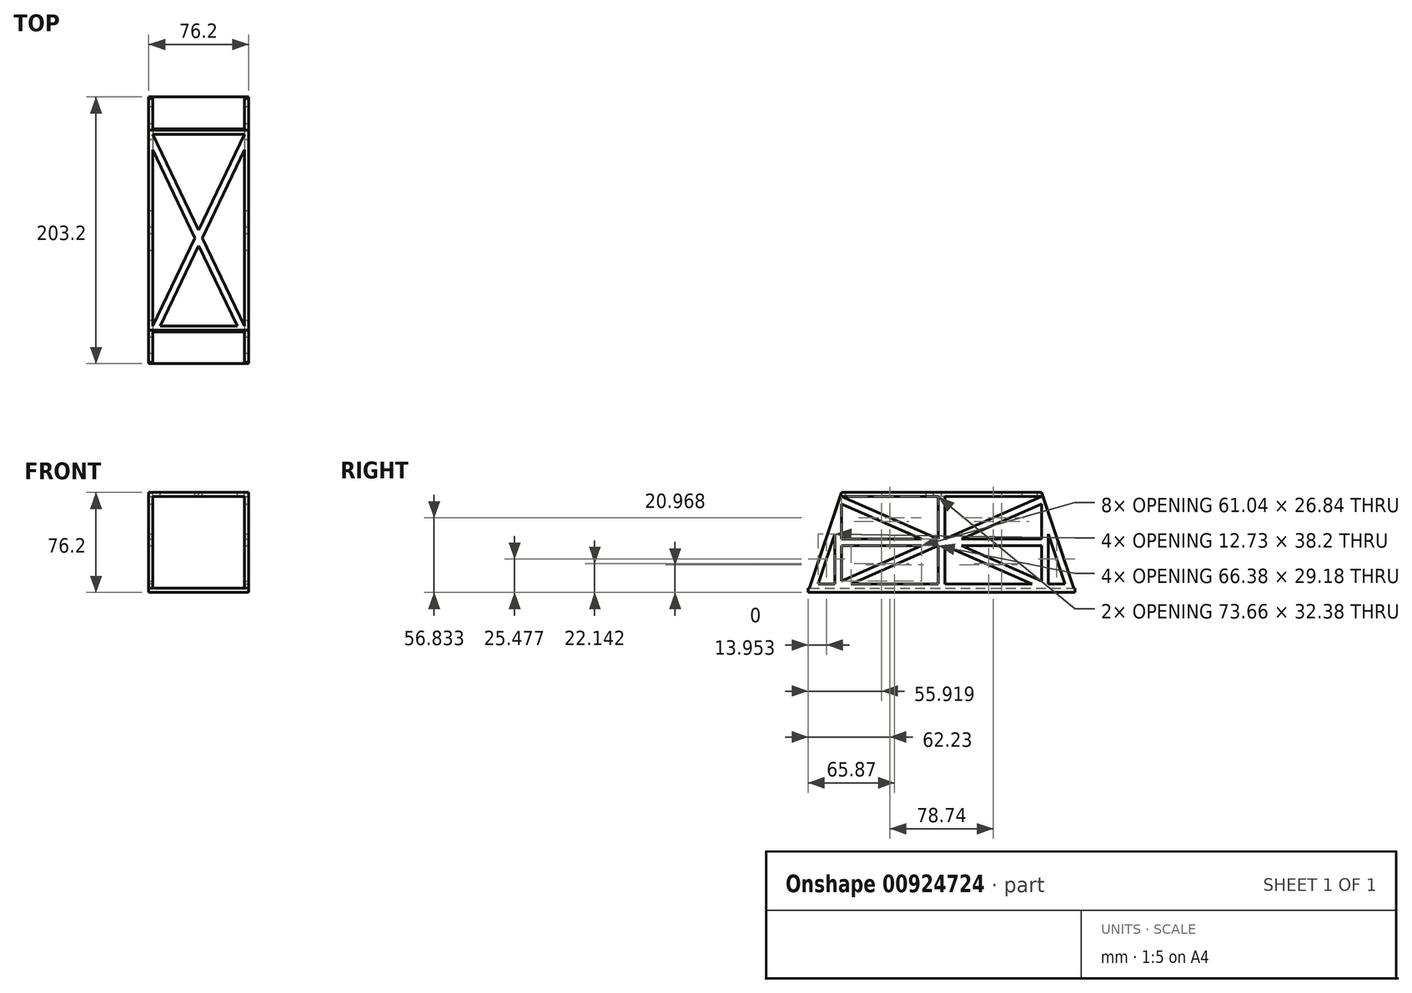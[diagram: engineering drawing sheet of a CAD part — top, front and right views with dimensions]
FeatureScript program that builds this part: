
annotation { "Feature Type Name" : "Feature", "Feature Type Description" : "" }
export const myFeature = defineFeature(function(context is Context, id is Id, definition is map)
    precondition{}
    {
        {
            var Q0;
            Q0=qCreatedBy(makeId("Right.planeOp"),FACE);
            var sketch = newSketch(context, id + "F0", { "sketchPlane" : qUnion([Q0])});
            skLineSegment(sketch, "E0", {"start": v(-101.6, -38.1) * mm, "end": v(101.6, -38.1) * mm});
            skLineSegment(sketch, "E1", {"start": v(-76.2, 38.1) * mm, "end": v(76.2, 38.1) * mm});
            skLineSegment(sketch, "E2", {"start": v(-76.2, 38.1) * mm, "end": v(-101.6, -38.1) * mm});
            skLineSegment(sketch, "E3", {"start": v(76.2, 38.1) * mm, "end": v(101.6, -38.1) * mm});
            skSolve(sketch);
        }
        {
            var Q0;
            Q0=makeQuery(id+"F0.imprint","IMPRINT",FACE,{"disambiguationData":[TD([[makeQuery(id+"F0.imprint","IMPRINT",EDGE,{"derivedFrom":sQuery(id+"F0.wireOp",EDGE,"E0")}),1.0]])]});
            extrude(context, id + "F1", {"entities" : qUnion([Q0]), "endBound" : BoundingType.SYMMETRIC, "depth" : 76.2 * mm, "offsetDistance" : 25.4 * mm});
        }
        {
            var Q0;
            Q0=makeQuery(id+"F1.opExtrude","CAP_FACE",FACE,{"disambiguationData":[OSD([sQuery(id+"F0.wireOp",EDGE,"E0"),sQuery(id+"F0.wireOp",EDGE,"E1"),sQuery(id+"F0.wireOp",EDGE,"E2"),sQuery(id+"F0.wireOp",EDGE,"E3")])],"isStart":false});
            var sketch = newSketch(context, id + "F2", { "sketchPlane" : qUnion([Q0])});
            skLineSegment(sketch, "E4.bottom", {"start": v(76.2, -34.92) * mm, "end": v(-76.2, -34.92) * mm});
            skLineSegment(sketch, "E4.top", {"start": v(76.2, 34.92) * mm, "end": v(-76.2, 34.92) * mm});
            skLineSegment(sketch, "E4.left", {"start": v(76.2, -34.92) * mm, "end": v(76.2, 34.92) * mm});
            skLineSegment(sketch, "E4.right", {"start": v(-76.2, -34.92) * mm, "end": v(-76.2, 34.92) * mm});
            skPoint(sketch, "E4.middle", {"position": v(0, 0) * mm});
            skLineSegment(sketch, "E5.bottom", {"start": v(2.54, -34.92) * mm, "end": v(-2.54, -34.92) * mm});
            skLineSegment(sketch, "E5.top", {"start": v(2.54, 34.92) * mm, "end": v(-2.54, 34.92) * mm});
            skLineSegment(sketch, "E5.left", {"start": v(2.54, -34.93) * mm, "end": v(2.54, 34.93) * mm});
            skLineSegment(sketch, "E5.right", {"start": v(-2.54, -34.93) * mm, "end": v(-2.54, 34.93) * mm});
            skLineSegment(sketch, "E6", {"start": v(-2.54, 0) * mm, "end": v(2.54, 0) * mm});
            skLineSegment(sketch, "E7.bottom", {"start": v(76.2, -2.54) * mm, "end": v(-76.2, -2.54) * mm});
            skLineSegment(sketch, "E7.top", {"start": v(76.2, 2.54) * mm, "end": v(-76.2, 2.54) * mm});
            skLineSegment(sketch, "E7.left", {"start": v(76.2, -2.54) * mm, "end": v(76.2, 2.54) * mm});
            skLineSegment(sketch, "E7.right", {"start": v(-76.2, -2.54) * mm, "end": v(-76.2, 2.54) * mm});
            skLineSegment(sketch, "E8", {"start": v(-76.2, 34.92) * mm, "end": v(-2.54, 2.54) * mm});
            skLineSegment(sketch, "E9", {"start": v(2.54, 2.54) * mm, "end": v(76.2, 34.92) * mm});
            skLineSegment(sketch, "E10", {"start": v(2.54, -2.54) * mm, "end": v(76.2, -34.92) * mm});
            skLineSegment(sketch, "E11", {"start": v(-2.54, -2.54) * mm, "end": v(-76.2, -34.92) * mm});
            skLineSegment(sketch, "E12", {"start": v(-76.2, -29.38) * mm, "end": v(-15.16, -2.54) * mm});
            skLineSegment(sketch, "E13", {"start": v(-15.16, 2.54) * mm, "end": v(-76.2, 29.38) * mm});
            skLineSegment(sketch, "E14", {"start": v(15.16, 2.54) * mm, "end": v(76.2, 29.38) * mm});
            skLineSegment(sketch, "E15", {"start": v(15.16, -2.54) * mm, "end": v(76.2, -29.38) * mm});
            skLineSegment(sketch, "E16", {"start": v(-81.28, -34.92) * mm, "end": v(-81.28, 6.48) * mm});
            skLineSegment(sketch, "E17", {"start": v(-81.28, 6.48) * mm, "end": v(-95.08, -34.92) * mm});
            skLineSegment(sketch, "E18", {"start": v(-95.08, -34.92) * mm, "end": v(-81.28, -34.92) * mm});
            skLineSegment(sketch, "E19.MirrorCS", {"start": v(81.28, -34.92) * mm, "end": v(81.28, 6.48) * mm});
            skLineSegment(sketch, "E20.MirrorCS", {"start": v(81.28, 6.48) * mm, "end": v(95.08, -34.92) * mm});
            skLineSegment(sketch, "E21.MirrorCS", {"start": v(95.08, -34.92) * mm, "end": v(81.28, -34.92) * mm});
            skSolve(sketch);
        }
        {
            var Q0;
            Q0=qCreatedBy(makeId("Front.planeOp"),FACE);
            var sketch = newSketch(context, id + "F3", { "sketchPlane" : qUnion([Q0])});
            skLineSegment(sketch, "E22.bottom", {"start": v(-34.93, -34.93) * mm, "end": v(34.93, -34.93) * mm});
            skLineSegment(sketch, "E22.top", {"start": v(-34.93, 34.93) * mm, "end": v(34.93, 34.93) * mm});
            skLineSegment(sketch, "E22.left", {"start": v(-34.93, -34.93) * mm, "end": v(-34.93, 34.93) * mm});
            skLineSegment(sketch, "E22.right", {"start": v(34.92, -34.93) * mm, "end": v(34.92, 34.93) * mm});
            skPoint(sketch, "E22.middle", {"position": v(0, 0) * mm});
            skSolve(sketch);
        }
        {
            var Q0;
            Q0=qSketchRegion(id+"F3",true);
            extrude(context, id + "F4", {"entities" : qUnion([Q0]), "operationType" : NewBodyOperationType.REMOVE, "endBound" : BoundingType.SYMMETRIC, "depth" : 254 * mm, "offsetDistance" : 25.4 * mm});
        }
        {
            var Q0;
            Q0=makeQuery(id+"F2.imprint","IMPRINT",FACE,{"disambiguationData":[TD([[makeQuery(id+"F2.imprint","IMPRINT",EDGE,{"derivedFrom":sQuery(id+"F2.wireOp",EDGE,"E16")}),1.0]])]});
            var Q1;
            {var subQ3=sQuery(id+"F2.wireOp",EDGE,"E12");Q1=makeQuery(id+"F2.imprint","IMPRINT",FACE,{"disambiguationData":[TD([[makeQuery(id+"F2.imprint","IMPRINT",EDGE,{"derivedFrom":subQ3}),1.0]])]});}
            var Q2;
            {var subQ3=sQuery(id+"F2.wireOp",EDGE,"E13");Q2=makeQuery(id+"F2.imprint","IMPRINT",FACE,{"disambiguationData":[TD([[makeQuery(id+"F2.imprint","IMPRINT",EDGE,{"derivedFrom":subQ3}),1.0]])]});}
            var Q3;
            {var subQ0=sQuery(id+"F2.wireOp",EDGE,"E8");Q3=makeQuery(id+"F2.imprint","IMPRINT",FACE,{"disambiguationData":[TD([[makeQuery(id+"F2.imprint","IMPRINT",EDGE,{"derivedFrom":subQ0}),1.0]])]});}
            var Q4;
            {var subQ0=sQuery(id+"F2.wireOp",EDGE,"E9");Q4=makeQuery(id+"F2.imprint","IMPRINT",FACE,{"disambiguationData":[TD([[makeQuery(id+"F2.imprint","IMPRINT",EDGE,{"derivedFrom":subQ0}),1.0]])]});}
            var Q5;
            {var subQ3=sQuery(id+"F2.wireOp",EDGE,"E14");Q5=makeQuery(id+"F2.imprint","IMPRINT",FACE,{"disambiguationData":[TD([[makeQuery(id+"F2.imprint","IMPRINT",EDGE,{"derivedFrom":subQ3}),-1.0]])]});}
            var Q6;
            {var subQ3=sQuery(id+"F2.wireOp",EDGE,"E15");Q6=makeQuery(id+"F2.imprint","IMPRINT",FACE,{"disambiguationData":[TD([[makeQuery(id+"F2.imprint","IMPRINT",EDGE,{"derivedFrom":subQ3}),1.0]])]});}
            var Q7;
            {var subQ0=sQuery(id+"F2.wireOp",EDGE,"E10");Q7=makeQuery(id+"F2.imprint","IMPRINT",FACE,{"disambiguationData":[TD([[makeQuery(id+"F2.imprint","IMPRINT",EDGE,{"derivedFrom":subQ0}),-1.0]])]});}
            var Q8;
            Q8=makeQuery(id+"F2.imprint","IMPRINT",FACE,{"disambiguationData":[TD([[makeQuery(id+"F2.imprint","IMPRINT",EDGE,{"derivedFrom":sQuery(id+"F2.wireOp",EDGE,"E19.MirrorCS")}),-1.0]])]});
            var Q9;
            {var subQ0=sQuery(id+"F2.wireOp",EDGE,"E11");Q9=makeQuery(id+"F2.imprint","IMPRINT",FACE,{"disambiguationData":[TD([[makeQuery(id+"F2.imprint","IMPRINT",EDGE,{"derivedFrom":subQ0}),1.0]])]});}
            extrude(context, id + "F5", {"entities" : qUnion([Q0, Q1, Q2, Q3, Q4, Q5, Q6, Q7, Q8, Q9]), "operationType" : NewBodyOperationType.REMOVE, "oppositeDirection" : true, "depth" : 76.2 * mm, "offsetDistance" : 25.4 * mm});
        }
        {
            var Q0;
            Q0=makeQuery(id+"F1.opExtrude","SWEPT_FACE",FACE,{"disambiguationData":[OSD([sQuery(id+"F0.wireOp",EDGE,"E1")])]});
            var sketch = newSketch(context, id + "F6", { "sketchPlane" : qUnion([Q0])});
            skLineSegment(sketch, "E23.bottom", {"start": v(34.92, -73.02) * mm, "end": v(-34.92, -73.02) * mm});
            skLineSegment(sketch, "E23.top", {"start": v(34.92, 73.02) * mm, "end": v(-34.92, 73.02) * mm});
            skLineSegment(sketch, "E23.left", {"start": v(-34.92, -73.02) * mm, "end": v(-34.92, 73.02) * mm});
            skLineSegment(sketch, "E23.right", {"start": v(34.92, -73.02) * mm, "end": v(34.92, 73.02) * mm});
            skPoint(sketch, "E23.middle", {"position": v(0, 0) * mm});
            skLineSegment(sketch, "E24", {"start": v(-34.92, 73.02) * mm, "end": v(34.92, -73.02) * mm});
            skLineSegment(sketch, "E25", {"start": v(34.92, 73.02) * mm, "end": v(-34.92, -73.02) * mm});
            skLineSegment(sketch, "E26", {"start": v(-34.93, 61.25) * mm, "end": v(29.3, -73.02) * mm});
            skLineSegment(sketch, "E27", {"start": v(34.92, 61.25) * mm, "end": v(-29.3, -73.02) * mm});
            skSolve(sketch);
        }
        {
            var Q0;
            {var subQ0=sQuery(id+"F6.wireOp",EDGE,"E23.top");Q0=makeQuery(id+"F6.imprint","IMPRINT",FACE,{"disambiguationData":[TD([[makeQuery(id+"F6.imprint","IMPRINT",EDGE,{"derivedFrom":subQ0}),1.0]])]});}
            var Q1;
            {var subQ1=sQuery(id+"F6.wireOp",EDGE,"E23.left");var subQ3=sQuery(id+"F6.wireOp",EDGE,"E26");var subQ4=makeQuery(id+"F6.imprint","INTERSECT",VERTEX,{"derivedFrom":[subQ1,subQ3]});Q1=makeQuery(id+"F6.imprint","IMPRINT",FACE,{"disambiguationData":[TD([[makeQuery(id+"F6.imprint","IMPRINT",EDGE,{"disambiguationData":[TD([[subQ4,-1.0]])],"derivedFrom":subQ3}),-1.0]])]});}
            var Q2;
            {var subQ1=sQuery(id+"F6.wireOp",EDGE,"E23.right");var subQ3=sQuery(id+"F6.wireOp",EDGE,"E27");var subQ4=makeQuery(id+"F6.imprint","INTERSECT",VERTEX,{"derivedFrom":[subQ1,subQ3]});Q2=makeQuery(id+"F6.imprint","IMPRINT",FACE,{"disambiguationData":[TD([[makeQuery(id+"F6.imprint","IMPRINT",EDGE,{"disambiguationData":[TD([[subQ4,-1.0]])],"derivedFrom":subQ3}),1.0]])]});}
            var Q3;
            {var subQ0=sQuery(id+"F6.wireOp",EDGE,"E26");var subQ1=sQuery(id+"F6.wireOp",EDGE,"E23.bottom");var subQ2=makeQuery(id+"F6.imprint","INTERSECT",VERTEX,{"derivedFrom":[subQ1,subQ0]});Q3=makeQuery(id+"F6.imprint","IMPRINT",FACE,{"disambiguationData":[TD([[makeQuery(id+"F6.imprint","IMPRINT",EDGE,{"disambiguationData":[TD([[subQ2,-1.0]])],"derivedFrom":subQ1}),-1.0]])]});}
            extrude(context, id + "F7", {"entities" : qUnion([Q0, Q1, Q2, Q3]), "operationType" : NewBodyOperationType.REMOVE, "oppositeDirection" : true, "depth" : 3.17 * mm, "offsetDistance" : 25.4 * mm});
        }
        {
            var Q0;
            Q0=makeQuery(id+"F1.opExtrude","CAP_FACE",FACE,{"disambiguationData":[OSD([sQuery(id+"F0.wireOp",EDGE,"E0"),sQuery(id+"F0.wireOp",EDGE,"E1"),sQuery(id+"F0.wireOp",EDGE,"E2"),sQuery(id+"F0.wireOp",EDGE,"E3")])],"isStart":false});
            var sketch = newSketch(context, id + "F8", { "sketchPlane" : qUnion([Q0])});
            skLineSegment(sketch, "E28.bottom", {"start": v(-101.6, -38.1) * mm, "end": v(-95.08, -38.1) * mm});
            skLineSegment(sketch, "E28.top", {"start": v(-101.6, -34.92) * mm, "end": v(-95.08, -34.92) * mm});
            skLineSegment(sketch, "E28.left", {"start": v(-101.6, -38.1) * mm, "end": v(-101.6, -34.92) * mm});
            skLineSegment(sketch, "E28.right", {"start": v(-95.08, -38.1) * mm, "end": v(-95.08, -34.92) * mm});
            skLineSegment(sketch, "E29.MirrorCS", {"start": v(101.6, -34.92) * mm, "end": v(95.08, -34.92) * mm});
            skLineSegment(sketch, "E30.MirrorCS", {"start": v(95.08, -38.1) * mm, "end": v(95.08, -34.92) * mm});
            skLineSegment(sketch, "E31.MirrorCS", {"start": v(101.6, -38.1) * mm, "end": v(95.08, -38.1) * mm});
            skLineSegment(sketch, "E32.MirrorCS", {"start": v(101.6, -38.1) * mm, "end": v(101.6, -34.92) * mm});
            skSolve(sketch);
        }
        {
            var Q0;
            Q0=qSketchRegion(id+"F8",true);
            extrude(context, id + "F9", {"entities" : qUnion([Q0]), "operationType" : NewBodyOperationType.ADD, "oppositeDirection" : true, "depth" : 76.2 * mm, "offsetDistance" : 25.4 * mm});
        }
        {
            var Q0;
            {var subQ0=sQuery(id+"F2.wireOp",EDGE,"E4.bottom");Q0=makeQuery(id+"F9.boolean.opBoolean","MERGE",FACE,{"derivedFrom":[makeQuery(id+"F5.boolean.opBoolean","MERGE",FACE,{"derivedFrom":[makeQuery(id+"F4.boolean.opBoolean","COPY",FACE,{"derivedFrom":makeQuery(id+"F4.opExtrude","SWEPT_FACE",FACE,{"disambiguationData":[OSD([sQuery(id+"F3.wireOp",EDGE,"E22.bottom")])]})})],"fromTools":[makeQuery(id+"F5.opExtrude","SWEPT_FACE",FACE,{"disambiguationData":[OSD([subQ0]),TDD([makeQuery(id+"F2.imprint","IMPRINT",EDGE,{"disambiguationData":[TD([[makeQuery(id+"F2.imprint","INTERSECT",VERTEX,{"derivedFrom":[subQ0,sQuery(id+"F2.wireOp",EDGE,"E4.left"),sQuery(id+"F2.wireOp",EDGE,"E10")]}),-1.0]])],"derivedFrom":subQ0})])]}),makeQuery(id+"F5.opExtrude","SWEPT_FACE",FACE,{"disambiguationData":[OSD([subQ0]),TDD([makeQuery(id+"F2.imprint","IMPRINT",EDGE,{"disambiguationData":[TD([[makeQuery(id+"F2.imprint","INTERSECT",VERTEX,{"derivedFrom":[subQ0,sQuery(id+"F2.wireOp",EDGE,"E4.right"),sQuery(id+"F2.wireOp",EDGE,"E11")]}),1.0]])],"derivedFrom":subQ0})])]}),makeQuery(id+"F5.opExtrude","SWEPT_FACE",FACE,{"disambiguationData":[OSD([sQuery(id+"F2.wireOp",EDGE,"E18")])]}),makeQuery(id+"F5.opExtrude","SWEPT_FACE",FACE,{"disambiguationData":[OSD([sQuery(id+"F2.wireOp",EDGE,"E21.MirrorCS")])]})]}),makeQuery(id+"F9.opExtrude","SWEPT_FACE",FACE,{"disambiguationData":[OSD([sQuery(id+"F8.wireOp",EDGE,"E28.top")])]}),makeQuery(id+"F9.opExtrude","SWEPT_FACE",FACE,{"disambiguationData":[OSD([sQuery(id+"F8.wireOp",EDGE,"E29.MirrorCS")])]})]});}
            var sketch = newSketch(context, id + "F10", { "sketchPlane" : qUnion([Q0])});
            skLineSegment(sketch, "E33.bottom", {"start": v(34.92, 95.08) * mm, "end": v(38.1, 95.08) * mm});
            skLineSegment(sketch, "E33.top", {"start": v(34.92, -95.08) * mm, "end": v(38.1, -95.08) * mm});
            skLineSegment(sketch, "E33.left", {"start": v(34.92, 95.08) * mm, "end": v(34.92, -95.08) * mm});
            skLineSegment(sketch, "E33.right", {"start": v(38.1, 95.08) * mm, "end": v(38.1, -95.08) * mm});
            skLineSegment(sketch, "E34.MirrorCS", {"start": v(-38.1, 95.08) * mm, "end": v(-38.1, -95.08) * mm});
            skLineSegment(sketch, "E35.MirrorCS", {"start": v(-34.92, 95.08) * mm, "end": v(-34.92, -95.08) * mm});
            skLineSegment(sketch, "E36", {"start": v(-38.1, -95.08) * mm, "end": v(-34.92, -95.08) * mm});
            skLineSegment(sketch, "E37", {"start": v(-38.1, 95.08) * mm, "end": v(-34.92, 95.08) * mm});
            skSolve(sketch);
        }
        {
            var Q0;
            Q0=qSketchRegion(id+"F10",true);
            extrude(context, id + "F11", {"entities" : qUnion([Q0]), "operationType" : NewBodyOperationType.ADD, "depth" : 3.17 * mm, "offsetDistance" : 25.4 * mm});
        }
        {
            var Q0;
            Q0=qSketchRegion(id+"F10",true);
            extrude(context, id + "F12", {"entities" : qUnion([Q0]), "operationType" : NewBodyOperationType.ADD, "depth" : 3.2 * mm, "offsetDistance" : 25.4 * mm});
        }
    });
